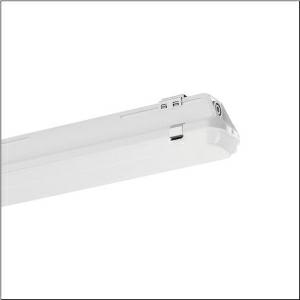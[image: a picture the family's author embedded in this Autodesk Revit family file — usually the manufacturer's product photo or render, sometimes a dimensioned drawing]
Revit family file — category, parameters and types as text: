
# Revit family: monsun_21_51fb107p440k
name_source: partatom
category: Lighting Fixtures
units: mm (PartAtom-declared; Revit-internal decimal feet)

## family parameters
Cut with Voids When Loaded = No
Host = Face
Light Source = No
Part Type = Normal
Room Calculation Point = No
Round Connector Dimension = Use Diameter
Shared = No

## types (1)
- Monsun 21 (1 x LED, 4400 lm, 24.8 W, 4000K)
    Apparent Load = 25 VA
    CIE Flux Codes = 47 77 93 94 100
    Color Rendering = 80
    Color Temperature = 4000K
    Default Elevation = 1800 mm
    Description = Monsun 21, damp-proof luminaire, chain hanger, primary optical cover: enclosure, of PMMA, light emission: direct distribution, primary light characteristic: symmetric, installation type: suspended mounting, surface-mounted, horizontal mounting, vertical mounting, LED, rated luminous flux: 4.400lm, luminous efficacy: 177lm/W, light colour: 840, colour temperature: 4000K, control gear: ON/OFF, with terminal, 3-pole, max. 2.5mm², mains connection: 220..240V, AC, 50/60Hz, rated input power: 25W, housing, of glass-fibre reinforced polyester, uncoated, bright grey, incl. chain hanger, length: 1.590mm, width: 90mm, height: 88mm, clip for enclosure, of stainless steel (V2A), ceiling mounting element, of stainless steel (V2A), chain hanger, of stainless steel (V2A), protection rating (complete): IP66, insulation class (complete): insulation class I (protective earthing), certification: CE, ENEC, VDE, UKCA, protection symbol: D, impact resistance: IK04, permissible operating ambient temperature: -25..+35°C, standard: EN 50419, EN 60598-2-1, corresponds to IFS (International Featured Standards) requirements for safety and quality in the food industry, for indoor or canopied outdoor use, no direct snow, no direct sun, no direct rain, LABS conformity tested according to VDMA 24364:2018-05, contact your sales advisor before using the luminaires in applications with unclear chemical exposure, large temperature fluctuations or condensation-forming humidity, packaging unit: 1 piece
    Height = 89 mm
    Lamp = 1 x LED
    Lamp Light Flux = 4400 lm
    Lamp Power = 24.8 W
    Lamp count = 1
    Length = 1590 mm
    Luminous efficacy = 177 lm/W
    Manufacturer = Siteco
    ModVariant = No
    Model = 51FB107P440K
    Mounting Place = Ceiling
    Mounting Type = Surface mounted
    Number of Poles = 1
    OnlyDefault = Yes
    Power Factor = 1
    Product Name = Monsun 21
    Product group = damp-proof luminaire
    ProductGroupID = 300
    Protection Class = Protection class I
    Protection Degree = IP 66
    RLX_Detail_Level = 1
    RLX_Emergency_Light_Flux = 0 lm
    RLX_Emergency_Type = 0
    RLX_Emergency_Type_DB = No
    RlxData = <blob elided: 88417 chars, md5=5e24929a>
    Socket = socket
    Standby Power = 0 W
    System Light Flux = 4400 lm
    System Power = 25 W
    Type Comments = Product without accessories
    Type Image = l_1319656.jpg
    URL = http://relux.com
    VarID = ---
    Voltage = 0 V
    Weight = 0.00 kg
    Width = 90 mm

## geometry (parser evidence)
native form markers: Blend x4, Sweep x14
no freeform markers — native parametric forms only
